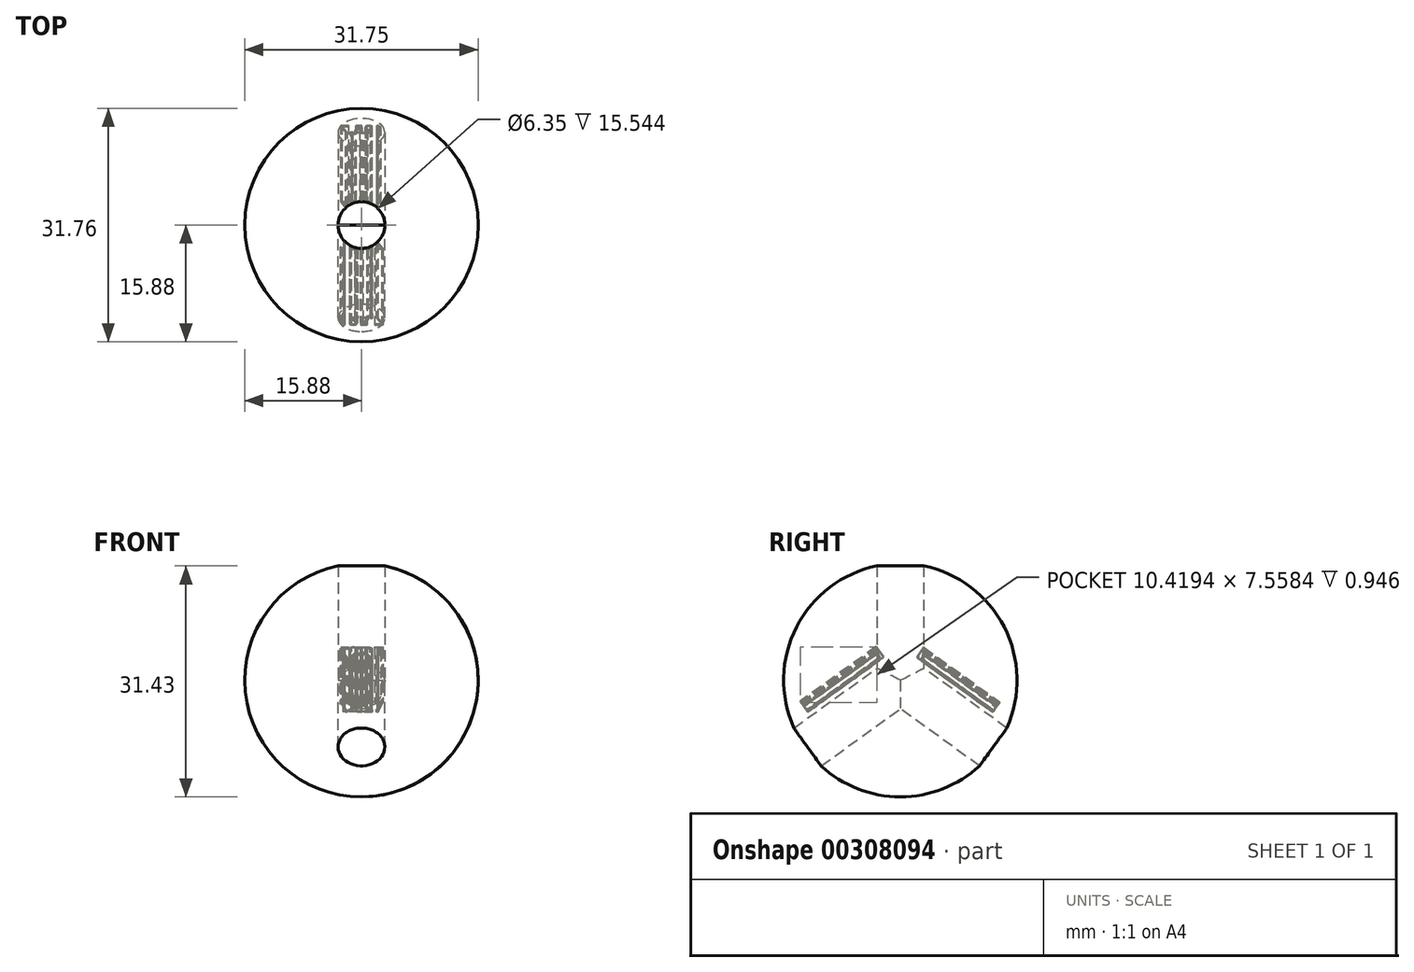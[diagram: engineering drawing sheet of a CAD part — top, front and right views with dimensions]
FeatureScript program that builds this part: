
annotation { "Feature Type Name" : "Feature", "Feature Type Description" : "" }
export const myFeature = defineFeature(function(context is Context, id is Id, definition is map)
    precondition{}
    {
        {
            var Q0;
            Q0=qCreatedBy(makeId("Front.planeOp"),FACE);
            var sketch = newSketch(context, id + "F0", { "sketchPlane" : qUnion([Q0])});
            skArc(sketch, "E0", {"start": v(0, 15.88) * mm, "mid": v(-15.88, 0) * mm, "end": v(0, -15.88) * mm});
            skLineSegment(sketch, "E1", {"start": v(0, 15.88) * mm, "end": v(0, -15.88) * mm});
            skSolve(sketch);
        }
        {
            var Q0;
            Q0=qCreatedBy(makeId("Top.planeOp"),FACE);
            var sketch = newSketch(context, id + "F1", { "sketchPlane" : qUnion([Q0])});
            skCircle(sketch, "E2", {"center": v(0, 0) * mm, "radius": 15.88 * mm});
            skSolve(sketch);
        }
        {
            var Q0;
            Q0=makeQuery(id+"F0.imprint","IMPRINT",FACE,{"disambiguationData":[TD([[makeQuery(id+"F0.imprint","IMPRINT",EDGE,{"derivedFrom":sQuery(id+"F0.wireOp",EDGE,"E0")}),1.0]])]});
            var Q1;
            Q1=sQuery(id+"F1.wireOp",EDGE,"E2");
            revolve(context, id + "F2", {"entities" : qUnion([Q0]), "axis" : qUnion([Q1]), "revolveType" : RevolveType.FULL});
        }
        {
            var Q0;
            Q0=qCreatedBy(makeId("Top.planeOp"),FACE);
            cPlane(context, id + "F3", {"entities" : qUnion([Q0]), "cplaneType" : CPlaneType.OFFSET, "offset" : 2 / 203.2 * mm, "width" : 152.4 * mm, "height" : 152.4 * mm});
        }
        {
            var Q0;
            Q0=qCreatedBy(id+"F3.planeOp",FACE);
            var sketch = newSketch(context, id + "F4", { "sketchPlane" : qUnion([Q0])});
            skCircle(sketch, "E3", {"center": v(0, 0) * mm, "radius": 3.18 * mm});
            skSolve(sketch);
        }
        {
            var Q0;
            Q0 = qSketchRegion(id + "F4", true);
            extrude(context, id + "F5", {"entities" : qUnion([Q0]), "depth" : 50.8 * mm});
        }
        {
            var Q0;
            Q0=qCreatedBy(makeId("Front.planeOp"),FACE);
            var sketch = newSketch(context, id + "F6", { "sketchPlane" : qUnion([Q0])});
            skLineSegment(sketch, "E4", {"start": v(0, 0) * mm, "end": v(0, 65.12) * mm, "construction": true});
            skLineSegment(sketch, "E5", {"start": v(0, 0) * mm, "end": v(58.07, 0) * mm, "construction": true});
            skSolve(sketch);
        }
        {
            var Q0;
            Q0=makeQuery(id+"F5.opExtrude","SWEPT_BODY",BODY,{"disambiguationData":[OSD([sQuery(id+"F4.wireOp",EDGE,"E3")])]});
            var Q1;
            Q1=sQuery(id+"F6.wireOp",EDGE,"E5");
            transform(context, id + "F7", {"entities" : qUnion([Q0]), "transformType" : TransformType.ROTATION, "transformAxis" : qUnion([Q1]), "angle" : 125.7 * degree, "makeCopy" : true});
        }
        {
            var Q0;
            Q0=makeQuery(id+"F5.opExtrude","SWEPT_BODY",BODY,{"disambiguationData":[OSD([sQuery(id+"F4.wireOp",EDGE,"E3")])]});
            var Q1;
            Q1=sQuery(id+"F6.wireOp",EDGE,"E5");
            transform(context, id + "F8", {"entities" : qUnion([Q0]), "transformType" : TransformType.ROTATION, "transformAxis" : qUnion([Q1]), "angle" : 125.7 * degree, "oppositeDirection" : true, "makeCopy" : true});
        }
        {
            var Q0;
            Q0=makeQuery(id+"F8.opPattern","COPY",FACE,{"derivedFrom":makeQuery(id+"F5.opExtrude","CAP_FACE",FACE,{"disambiguationData":[OSD([sQuery(id+"F4.wireOp",EDGE,"E3")])],"isStart":false}),"instanceName":"1"});
            cPlane(context, id + "F9", {"entities" : qUnion([Q0]), "cplaneType" : CPlaneType.OFFSET, "offset" : 38.1 * mm, "oppositeDirection" : true, "width" : 152.4 * mm, "height" : 152.4 * mm});
        }
        {
            var Q0;
            Q0=qCreatedBy(id+"F9.planeOp",FACE);
            var sketch = newSketch(context, id + "F10", { "sketchPlane" : qUnion([Q0])});
            skText(sketch, "E6", { "text": "125.7", "fontName": "OpenSans-Regular.ttf"});
            const initialGuessF10  = {"E6": [-0.0029, 0.00384, 1, 0, 0.00164]};
            skSetInitialGuess(sketch, initialGuessF10);
            skSolve(sketch);
        }
        {
            var Q0;
            Q0 = qSketchRegion(id + "F10", true);
            extrude(context, id + "F11", {"entities" : qUnion([Q0]), "operationType" : NewBodyOperationType.REMOVE, "oppositeDirection" : true, "depth" : 12.7 * mm});
        }
        {
            var Q0;
            Q0=makeQuery(id+"F7.opPattern","COPY",FACE,{"derivedFrom":makeQuery(id+"F5.opExtrude","CAP_FACE",FACE,{"disambiguationData":[OSD([sQuery(id+"F4.wireOp",EDGE,"E3")])],"isStart":false}),"instanceName":"1"});
            cPlane(context, id + "F12", {"entities" : qUnion([Q0]), "cplaneType" : CPlaneType.OFFSET, "offset" : 38.1 * mm, "oppositeDirection" : true, "width" : 152.4 * mm, "height" : 152.4 * mm});
        }
        {
            var Q0;
            Q0=qCreatedBy(id+"F12.planeOp",FACE);
            var sketch = newSketch(context, id + "F13", { "sketchPlane" : qUnion([Q0])});
            skText(sketch, "E7", { "text": "125.7", "fontName": "OpenSans-Regular.ttf"});
            const initialGuessF13  = {"E7": [-0.00315, 0.00386, 1, 0, 0.00175]};
            skSetInitialGuess(sketch, initialGuessF13);
            skSolve(sketch);
        }
        {
            var Q0;
            Q0 = qSketchRegion(id + "F13", true);
            extrude(context, id + "F14", {"entities" : qUnion([Q0]), "operationType" : NewBodyOperationType.REMOVE, "oppositeDirection" : true, "depth" : 12.7 * mm});
        }
        {
            var Q0;
            Q0=makeQuery(id+"F5.opExtrude","SWEPT_BODY",BODY,{"disambiguationData":[OSD([sQuery(id+"F4.wireOp",EDGE,"E3")])]});
            var Q1;
            Q1=makeQuery(id+"F7.opPattern","COPY",BODY,{"derivedFrom":makeQuery(id+"F5.opExtrude","SWEPT_BODY",BODY,{"disambiguationData":[OSD([sQuery(id+"F4.wireOp",EDGE,"E3")])]}),"instanceName":"1"});
            var Q2;
            Q2=makeQuery(id+"F8.opPattern","COPY",BODY,{"derivedFrom":makeQuery(id+"F5.opExtrude","SWEPT_BODY",BODY,{"disambiguationData":[OSD([sQuery(id+"F4.wireOp",EDGE,"E3")])]}),"instanceName":"1"});
            var Q3;
            Q3=makeQuery(id+"F2.opRevolve","SWEPT_BODY",BODY,{"disambiguationData":[OSD([sQuery(id+"F0.wireOp",EDGE,"E0"),sQuery(id+"F0.wireOp",EDGE,"E1")])]});
            booleanBodies(context, id + "F15", {"operationType" : BooleanOperationType.SUBTRACTION, "tools" : qUnion([Q0, Q1, Q2]), "targets" : qUnion([Q3])});
        }
        {
            var Q0;
            Q0=makeQuery(id+"F2.opRevolve","SWEPT_BODY",BODY,{"disambiguationData":[OSD([sQuery(id+"F0.wireOp",EDGE,"E0"),sQuery(id+"F0.wireOp",EDGE,"E1")])]});
            transform(context, id + "F16", {"entities" : qUnion([Q0]), "transformType" : TransformType.TRANSLATION_3D, "dx" : 0 * mm, "dy" : 0 * mm, "dz" : 0 * mm, "makeCopy" : true});
        }
        {
            var Q0;
            Q0=makeQuery(id+"F16.opPattern","COPY",BODY,{"derivedFrom":makeQuery(id+"F2.opRevolve","SWEPT_BODY",BODY,{"disambiguationData":[OSD([sQuery(id+"F0.wireOp",EDGE,"E0"),sQuery(id+"F0.wireOp",EDGE,"E1")])]}),"instanceName":"1"});
            deleteBodies(context, id + "F17", {"entities" : qUnion([Q0])});
        }
        {
            var Q0;
            Q0=makeQuery(id+"F2.opRevolve","SWEPT_BODY",BODY,{"disambiguationData":[OSD([sQuery(id+"F0.wireOp",EDGE,"E0"),sQuery(id+"F0.wireOp",EDGE,"E1")])]});
            transform(context, id + "F18", {"entities" : qUnion([Q0]), "transformType" : TransformType.TRANSLATION_3D, "dx" : 0 * mm, "dy" : 0 * mm, "dz" : 0 * mm, "makeCopy" : true});
        }
        {
            var Q0;
            Q0=makeQuery(id+"F18.opPattern","COPY",BODY,{"derivedFrom":makeQuery(id+"F2.opRevolve","SWEPT_BODY",BODY,{"disambiguationData":[OSD([sQuery(id+"F0.wireOp",EDGE,"E0"),sQuery(id+"F0.wireOp",EDGE,"E1")])]}),"instanceName":"1"});
            deleteBodies(context, id + "F19", {"entities" : qUnion([Q0])});
        }
    });
